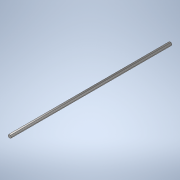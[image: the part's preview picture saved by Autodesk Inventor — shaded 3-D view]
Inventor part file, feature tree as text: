
AUTODESK INVENTOR PART (.ipt)
format: ipt  version: 2020 (Build 240168000, 168)  size: 108,032 bytes
history: native  units: in
note: dims shown in document units (in); Inventor stores cm internally (conversion verified against a paired STEP export)
features: extrude x1, sketch x1
ambient origin geometry x8: Origin, YZ Plane, XZ Plane, XY Plane, X Axis, Y Axis, Z Axis, Center Point
bodies: Solid1 (feature_tree)
feature tree (2):
  extrude  "Extrusion1"  Depth=28.0in TaperAngle=0.0deg
  sketch  "Sketch1"  dims[d0=0.5in d1=28.0in d2=0.0in]
